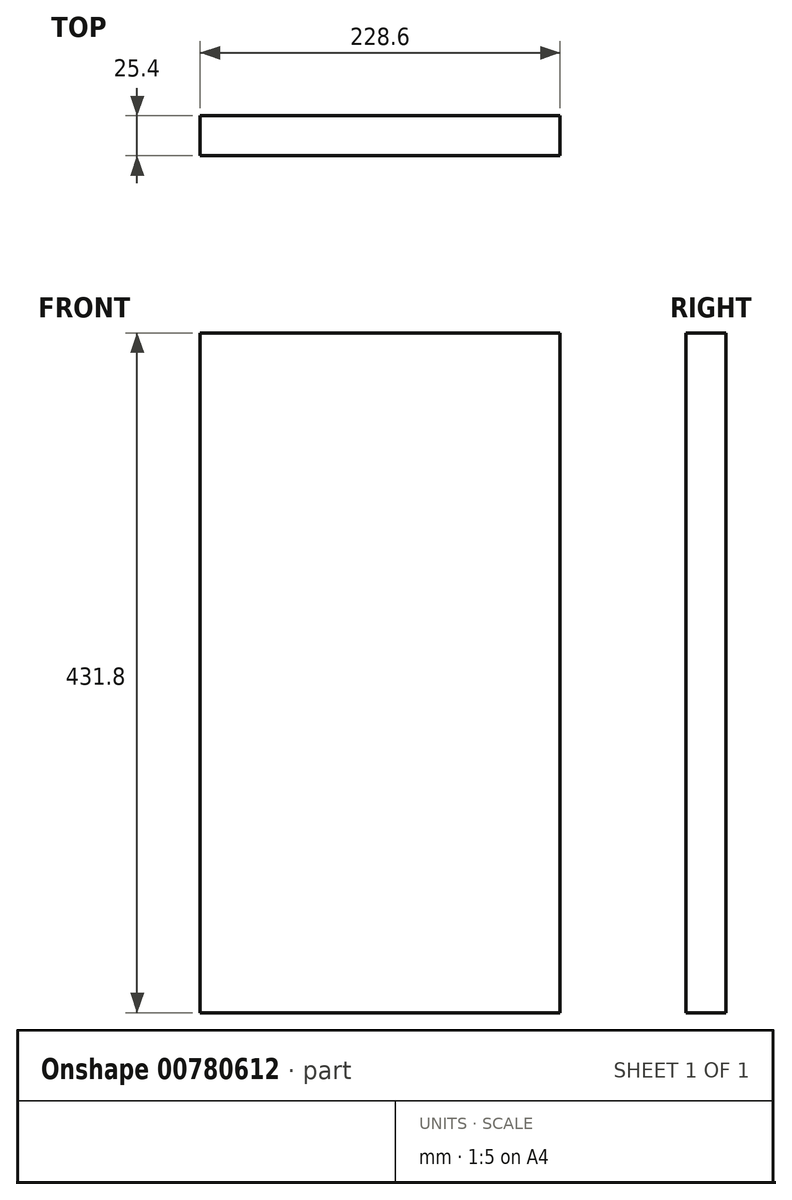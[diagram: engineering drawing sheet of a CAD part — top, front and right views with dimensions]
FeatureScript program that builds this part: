
annotation { "Feature Type Name" : "Feature", "Feature Type Description" : "" }
export const myFeature = defineFeature(function(context is Context, id is Id, definition is map)
    precondition{}
    {
        {
            var Q0;
            Q0=qCreatedBy(makeId("Front.planeOp"),FACE);
            var sketch = newSketch(context, id + "F0", { "sketchPlane" : qUnion([Q0])});
            skLineSegment(sketch, "E0.bottom", {"start": v(114.3, -215.9) * mm, "end": v(-114.3, -215.9) * mm});
            skLineSegment(sketch, "E0.top", {"start": v(114.3, 215.9) * mm, "end": v(-114.3, 215.9) * mm});
            skLineSegment(sketch, "E0.left", {"start": v(114.3, -215.9) * mm, "end": v(114.3, 215.9) * mm});
            skLineSegment(sketch, "E0.right", {"start": v(-114.3, -215.9) * mm, "end": v(-114.3, 215.9) * mm});
            skPoint(sketch, "E0.middle", {"position": v(0, 0) * mm});
            skSolve(sketch);
        }
        {
            var Q0;
            Q0=qSketchRegion(id+"F0",true);
            extrude(context, id + "F1", {"entities" : qUnion([Q0]), "depth" : 25.4 * mm, "offsetDistance" : 25.4 * mm});
        }
    });
